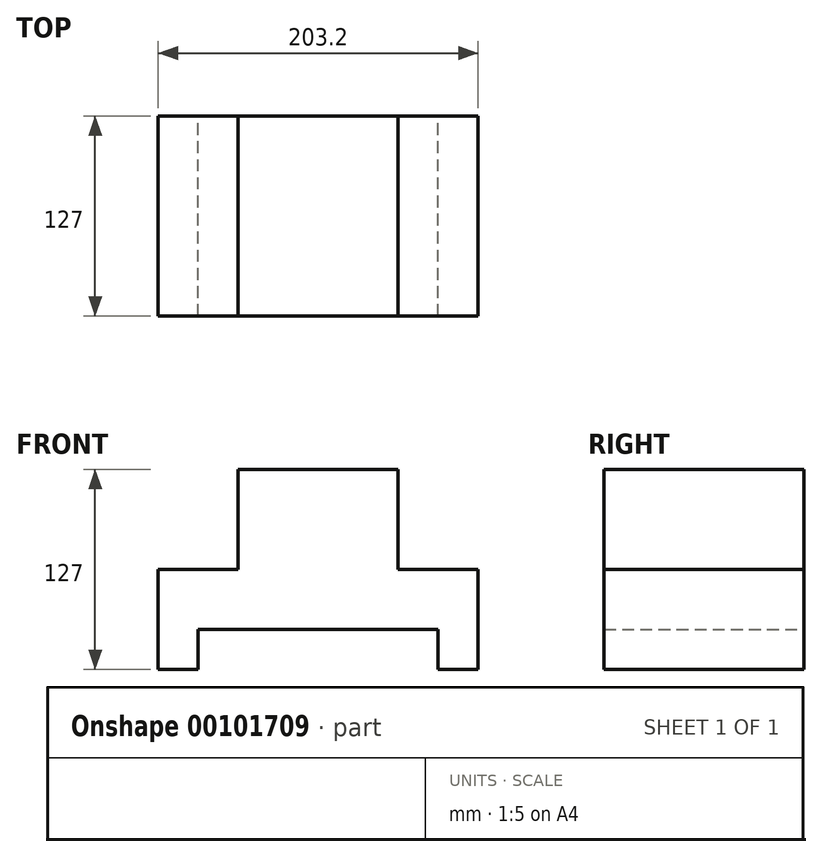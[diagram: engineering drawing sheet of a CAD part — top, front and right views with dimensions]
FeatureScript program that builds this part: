
annotation { "Feature Type Name" : "Feature", "Feature Type Description" : "" }
export const myFeature = defineFeature(function(context is Context, id is Id, definition is map)
    precondition{}
    {
        {
            var Q0;
            Q0=qCreatedBy(makeId("Front.planeOp"),FACE);
            var sketch = newSketch(context, id + "F0", { "sketchPlane" : qUnion([Q0])});
            skLineSegment(sketch, "E0", {"start": v(-95.1, -70.36) * mm, "end": v(-69.7, -70.36) * mm});
            skLineSegment(sketch, "E1", {"start": v(-69.7, -70.36) * mm, "end": v(-69.7, -44.96) * mm});
            skLineSegment(sketch, "E2", {"start": v(-69.7, -44.96) * mm, "end": v(82.7, -44.96) * mm});
            skLineSegment(sketch, "E3", {"start": v(82.7, -44.96) * mm, "end": v(82.7, -70.36) * mm});
            skLineSegment(sketch, "E4", {"start": v(82.7, -70.36) * mm, "end": v(108.1, -70.36) * mm});
            skLineSegment(sketch, "E5", {"start": v(108.1, -70.36) * mm, "end": v(108.1, -6.86) * mm});
            skLineSegment(sketch, "E6", {"start": v(108.1, -6.86) * mm, "end": v(57.3, -6.86) * mm});
            skLineSegment(sketch, "E7", {"start": v(57.3, -6.86) * mm, "end": v(57.3, 56.64) * mm});
            skLineSegment(sketch, "E8", {"start": v(57.3, 56.64) * mm, "end": v(-44.3, 56.64) * mm});
            skLineSegment(sketch, "E9", {"start": v(-44.3, 56.64) * mm, "end": v(-44.3, -6.86) * mm});
            skLineSegment(sketch, "E10", {"start": v(-44.3, -6.86) * mm, "end": v(-95.1, -6.86) * mm});
            skLineSegment(sketch, "E11", {"start": v(-95.1, -6.86) * mm, "end": v(-95.1, -70.36) * mm});
            skSolve(sketch);
        }
        {
            var Q0;
            Q0=makeQuery(id+"F0.imprint","IMPRINT",FACE,{"disambiguationData":[TD([[makeQuery(id+"F0.imprint","IMPRINT",EDGE,{"derivedFrom":sQuery(id+"F0.wireOp",EDGE,"E0")}),1.0]])]});
            extrude(context, id + "F1", {"entities" : qUnion([Q0]), "depth" : 127 * mm});
        }
    });
